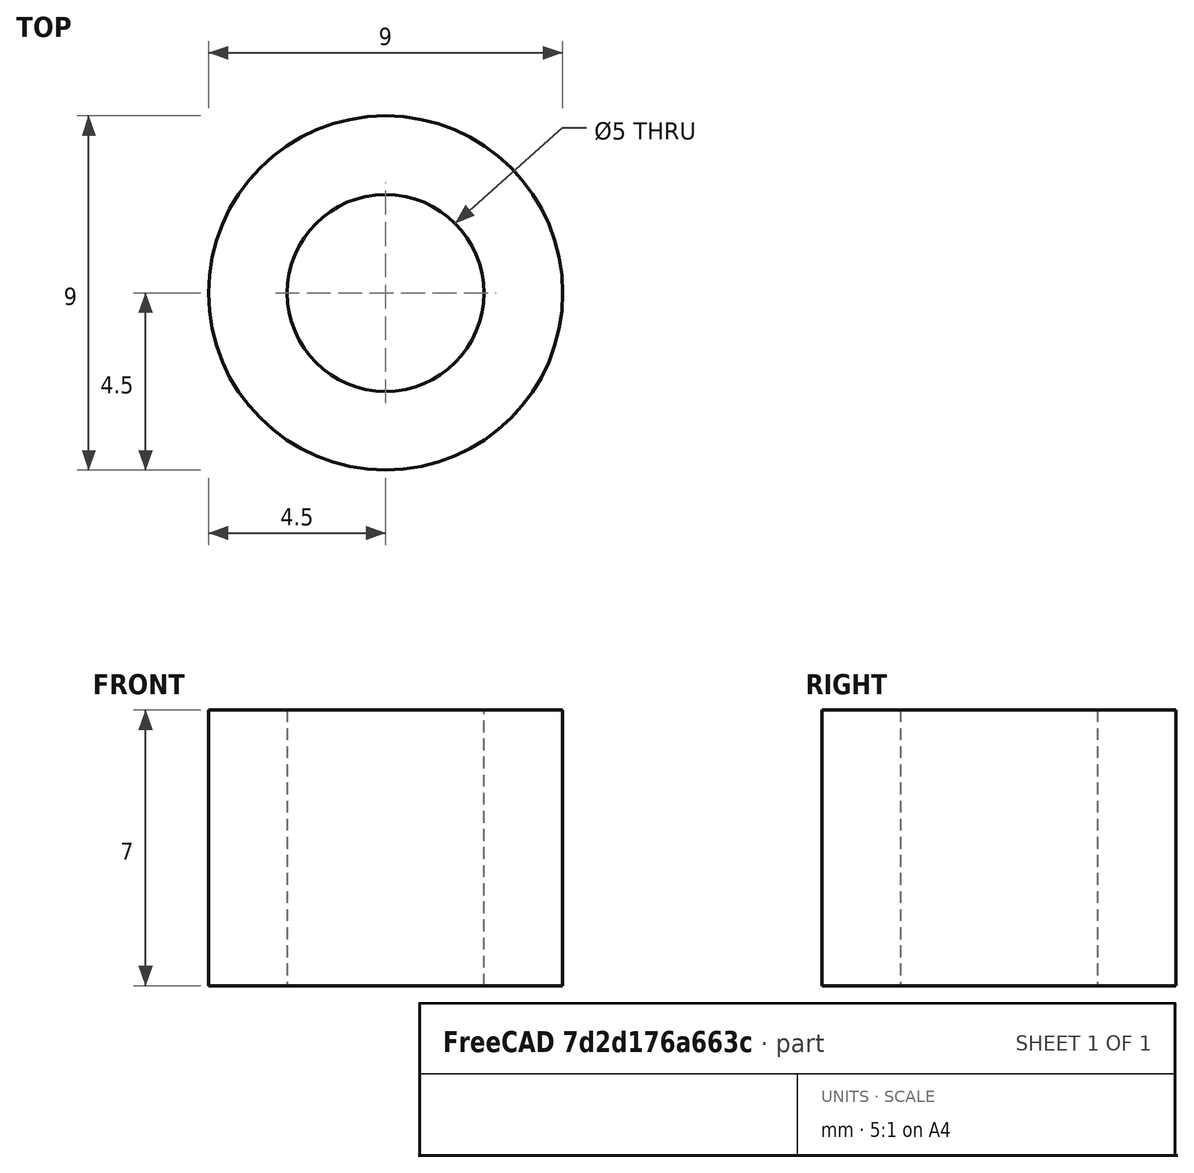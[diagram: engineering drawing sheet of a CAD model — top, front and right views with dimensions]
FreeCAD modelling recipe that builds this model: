
FCSTD DOCUMENT  (FreeCAD 0.19R24276 (Git))
Label: Vtulka_9x5x7
License: All rights reserved
LicenseURL: http://en.wikipedia.org/wiki/All_rights_reserved
objects: Sketcher::SketchObject×1, PartDesign::Pad×1, PartDesign::Body×1
note: 4 computed .brp shape members not serialized (recipe doc carries the construction recipe); baked Part::Feature solids carry a one-line shape summary decoded from their .brp

FEATURE [Sketcher::SketchObject] Sketch
  FullyConstrained = true
  MapMode = 5
  Support = -> [XY_Plane]
  sketch-geometry (2):
    g0: Circle CenterX=0 CenterY=0 CenterZ=0 NormalX=0 NormalY=0 NormalZ=1 AngleXU=0 Radius=2.5
    g1: Circle CenterX=0 CenterY=0 CenterZ=0 NormalX=0 NormalY=0 NormalZ=1 AngleXU=0 Radius=4.5
  constraints (4):
    c: Coincident(g0,g-1)
    c: Coincident(g1,g0)
    c: Diameter(g0) = 5
    c: Diameter(g1) = 9
FEATURE [PartDesign::Pad] Pad
  Direction = (1,1,1)
  Length = 7
  Length2 = 100
  Profile = -> Sketch
  Type = 0
FEATURE [PartDesign::Body] Body
  Group = -> [Sketch,Pad]
  Origin = -> Origin
  Tip = -> Pad
